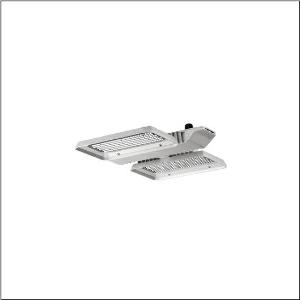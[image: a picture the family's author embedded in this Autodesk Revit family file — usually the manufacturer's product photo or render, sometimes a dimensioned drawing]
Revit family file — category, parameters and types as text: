
# Revit family: highbay_11_51hla1d14fca
name_source: partatom
category: Lighting Fixtures
units: mm (PartAtom-declared; Revit-internal decimal feet)

## family parameters
Cut with Voids When Loaded = No
Host = Face
Light Source = No
Part Type = Normal
Room Calculation Point = No
Round Connector Dimension = Use Diameter
Shared = No

## types (1)
- --- (1 x LED, 14060 lm, 81.2 W, 4000K)
    Apparent Load = 81 VA
    CIE Flux Codes = 88 95 99 100 99
    Color Rendering = 80
    Color Temperature = 4000K
    Default Elevation = 1800 mm
    Description = Highbay 11, LED high bay luminaire, primary light control with lens, of PMMA, light emission: direct distribution, primary light characteristic: symmetric, installation type: surface-mounted, suspended mounting, for 1x 2x LED, rated luminous flux: 14.060lm, luminous efficacy: 173lm/W, light colour: 840, colour temperature: 4000K, control gear: ECG DALI, with terminal, 5-pole, max. 2.5mm², mains connection: 230..240V, AC, 50/60Hz, rated input power: 81W, LED unit, of diecast aluminium, unplated, bead blasted, silver, length: 470mm, width: 500mm, height: 65mm, housing, of diecast aluminium, uncoated, bead blasted, silver, protection rating (complete): IP65, insulation class (complete): insulation class I (protective earthing), certification: CE, ENEC, VDE, UKCA, protection symbol: D, impact resistance: IK08 with glass or PC cover, permissible operating ambient temperature: -35..+55°C, reducing of maximum allowable ambient temperature of 5°C with ceiling mounting, corresponds to IFS (International Featured Standards) requirements for safety and quality in the food industry, packaging unit: 1 piece
    Height = 95 mm
    Lamp = 1 x LED
    Lamp Light Flux = 14060 lm
    Lamp Power = 81.2 W
    Lamp count = 1
    Length = 468 mm
    Luminous efficacy = 173 lm/W
    Manufacturer = Siteco
    ModVariant = No
    Model = 51HLA1D14FCA
    Mounting Place = Ceiling
    Mounting Type = Pendant
    Number of Poles = 1
    OnlyDefault = Yes
    Power Factor = 1
    Product Name = Highbay 11
    Product group = LED high bay luminaire
    ProductGroupID = 903
    Protection Class = Protection class I
    Protection Degree = IP 65
    RLX_Detail_Level = 1
    RLX_Emergency_Light_Flux = 0 lm
    RLX_Emergency_Type = 0
    RLX_Emergency_Type_DB = No
    RlxData = <blob elided: 89833 chars, md5=da19f703>
    Socket = socket
    Standby Power = 0 W
    System Light Flux = 14060 lm
    System Power = 81 W
    Type Comments = factory setting: luminous flux: 100 % | dim-lin: 254 | 460 mA
    Type Image = l_1003425.jpg
    URL = http://relux.com
    VarID = @adj_146231
    Voltage = 0 V
    Weight = 0.00 kg
    Width = 501 mm

## geometry (parser evidence)
native form markers: Blend x4, Sweep x13
no freeform markers — native parametric forms only
